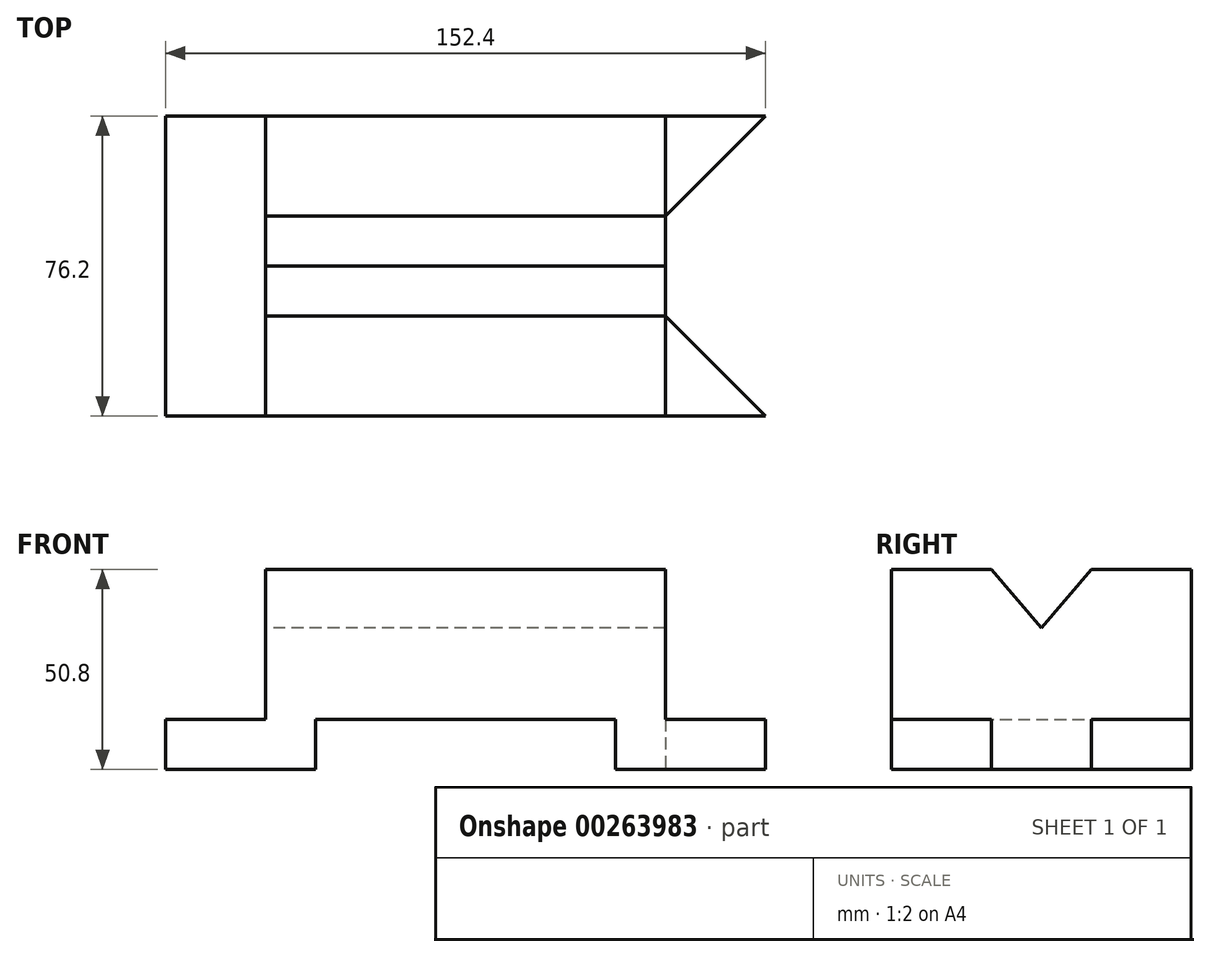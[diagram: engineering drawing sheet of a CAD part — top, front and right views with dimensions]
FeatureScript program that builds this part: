
annotation { "Feature Type Name" : "Feature", "Feature Type Description" : "" }
export const myFeature = defineFeature(function(context is Context, id is Id, definition is map)
    precondition{}
    {
        {
            var Q0;
            Q0=qCreatedBy(makeId("Front.planeOp"),FACE);
            var sketch = newSketch(context, id + "F0", { "sketchPlane" : qUnion([Q0])});
            skLineSegment(sketch, "E0", {"start": v(0, 0) * mm, "end": v(0, 12.7) * mm});
            skLineSegment(sketch, "E1", {"start": v(0, 12.7) * mm, "end": v(25.4, 12.7) * mm});
            skLineSegment(sketch, "E2", {"start": v(25.4, 12.7) * mm, "end": v(25.4, 50.8) * mm});
            skLineSegment(sketch, "E3", {"start": v(25.4, 50.8) * mm, "end": v(127, 50.8) * mm});
            skLineSegment(sketch, "E4", {"start": v(127, 50.8) * mm, "end": v(127, 0) * mm});
            skLineSegment(sketch, "E5", {"start": v(127, 0) * mm, "end": v(114.3, 0) * mm});
            skLineSegment(sketch, "E6", {"start": v(114.3, 0) * mm, "end": v(114.3, 12.7) * mm});
            skLineSegment(sketch, "E7", {"start": v(114.3, 12.7) * mm, "end": v(38.1, 12.7) * mm});
            skLineSegment(sketch, "E8", {"start": v(38.1, 12.7) * mm, "end": v(38.1, 0) * mm});
            skLineSegment(sketch, "E9", {"start": v(38.1, 0) * mm, "end": v(0, 0) * mm});
            skSolve(sketch);
        }
        {
            var Q0;
            Q0=makeQuery(id+"F0.imprint","IMPRINT",FACE,{"disambiguationData":[TD([[makeQuery(id+"F0.imprint","IMPRINT",EDGE,{"derivedFrom":sQuery(id+"F0.wireOp",EDGE,"E0")}),-1.0]])]});
            extrude(context, id + "F1", {"entities" : qUnion([Q0]), "depth" : 76.2 * mm});
        }
        {
            var Q0;
            Q0=makeQuery(id+"F1.opExtrude","SWEPT_FACE",FACE,{"disambiguationData":[OSD([sQuery(id+"F0.wireOp",EDGE,"E2")])]});
            var sketch = newSketch(context, id + "F2", { "sketchPlane" : qUnion([Q0])});
            skLineSegment(sketch, "E10", {"start": v(0, 50.8) * mm, "end": v(25.4, 50.8) * mm});
            skLineSegment(sketch, "E11", {"start": v(25.4, 50.8) * mm, "end": v(38.1, 35.98) * mm});
            skLineSegment(sketch, "E12", {"start": v(38.1, 35.98) * mm, "end": v(50.8, 50.8) * mm});
            skLineSegment(sketch, "E13", {"start": v(50.8, 50.8) * mm, "end": v(76.2, 50.8) * mm});
            skSolve(sketch);
        }
        {
            var Q0;
            {var subQ0=sQuery(id+"F2.wireOp",EDGE,"E11");Q0=makeQuery(id+"F2.imprint","IMPRINT",FACE,{"disambiguationData":[TD([[makeQuery(id+"F2.imprint","IMPRINT",EDGE,{"derivedFrom":subQ0}),1.0]])]});}
            extrude(context, id + "F3", {"entities" : qUnion([Q0]), "operationType" : NewBodyOperationType.REMOVE, "oppositeDirection" : true, "depth" : 152.4 * mm});
        }
        {
            var Q0;
            Q0=makeQuery(id+"F1.opExtrude","SWEPT_FACE",FACE,{"disambiguationData":[OSD([sQuery(id+"F0.wireOp",EDGE,"E5")])]});
            var sketch = newSketch(context, id + "F4", { "sketchPlane" : qUnion([Q0])});
            skLineSegment(sketch, "E14", {"start": v(127, 76.2) * mm, "end": v(127, 50.8) * mm});
            skLineSegment(sketch, "E15", {"start": v(127, 50.8) * mm, "end": v(152.4, 76.2) * mm});
            skLineSegment(sketch, "E16", {"start": v(127, 76.2) * mm, "end": v(152.4, 76.2) * mm});
            skLineSegment(sketch, "E17", {"start": v(127, 0) * mm, "end": v(152.4, 0) * mm});
            skLineSegment(sketch, "E18", {"start": v(152.4, 0) * mm, "end": v(127, 25.4) * mm});
            skLineSegment(sketch, "E19", {"start": v(127, 25.4) * mm, "end": v(127, 0) * mm});
            skSolve(sketch);
        }
        {
            var Q0;
            Q0 = qSketchRegion(id + "F4", true);
            extrude(context, id + "F5", {"entities" : qUnion([Q0]), "operationType" : NewBodyOperationType.ADD, "oppositeDirection" : true, "depth" : 12.7 * mm});
        }
    });
